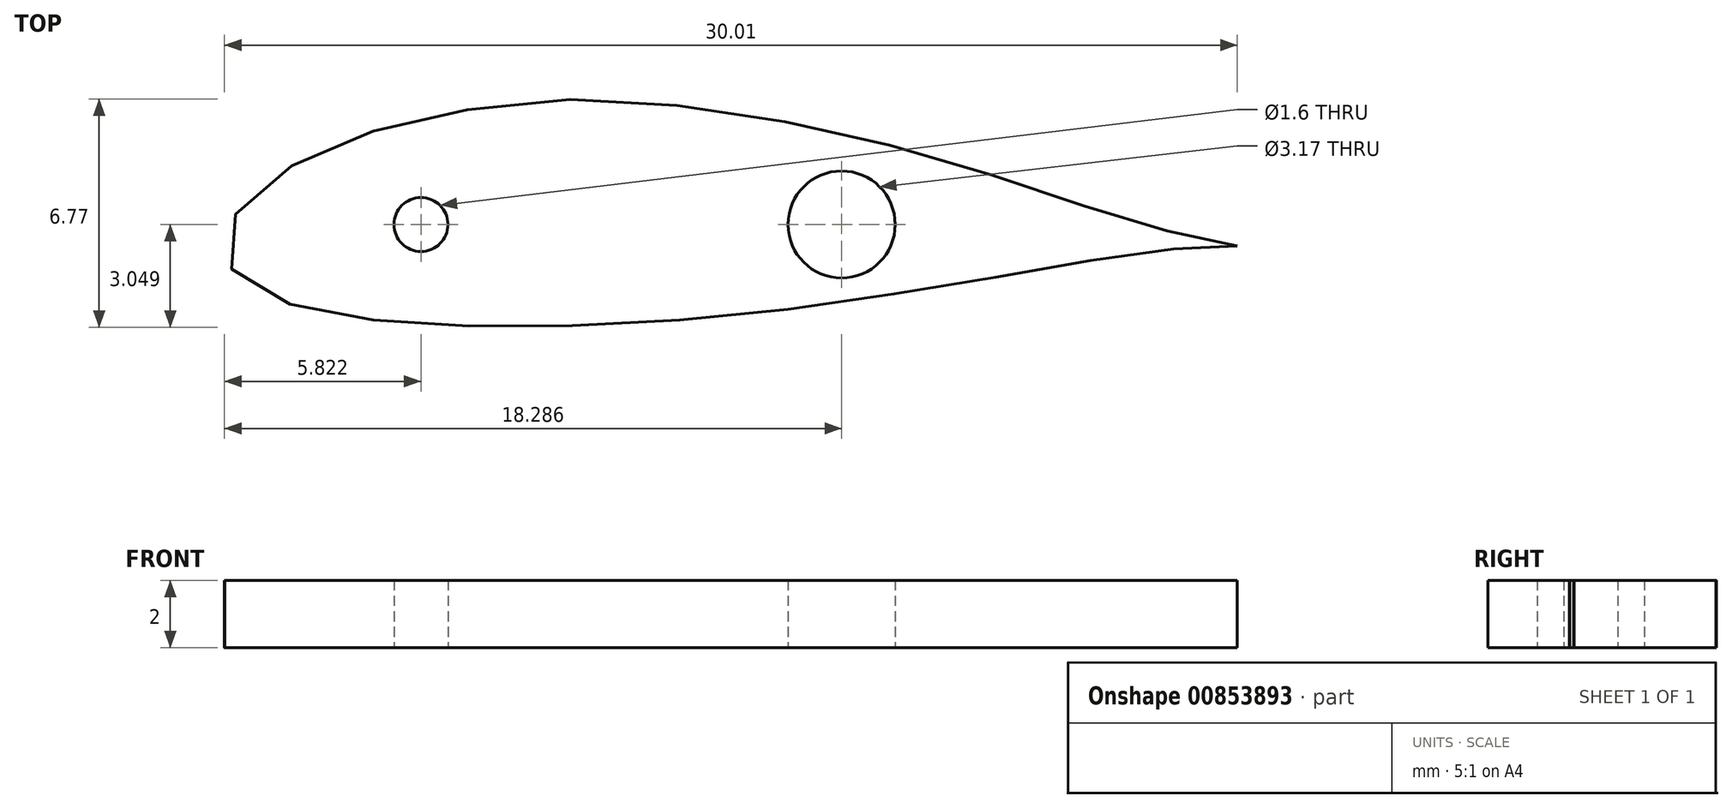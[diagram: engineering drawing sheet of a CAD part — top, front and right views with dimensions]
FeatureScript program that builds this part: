
annotation { "Feature Type Name" : "Feature", "Feature Type Description" : "" }
export const myFeature = defineFeature(function(context is Context, id is Id, definition is map)
    precondition{}
    {
        {
            var Q0;
            Q0=qCreatedBy(makeId("Top.planeOp"),FACE);
            var sketch = newSketch(context, id + "F0", { "sketchPlane" : qUnion([Q0])});
            skPoint(sketch, "E0", {"position": v(-51.28, 25.16) * mm});
            skPoint(sketch, "E1", {"position": v(-51.19, 25.72) * mm});
            skPoint(sketch, "E2", {"position": v(-51.29, 25.4) * mm});
            skPoint(sketch, "E3", {"position": v(-51.02, 26) * mm});
            skPoint(sketch, "E4", {"position": v(-50.8, 26.3) * mm});
            skPoint(sketch, "E5", {"position": v(-50.53, 26.6) * mm});
            skPoint(sketch, "E6", {"position": v(-50.17, 26.92) * mm});
            skPoint(sketch, "E7", {"position": v(-49.77, 27.22) * mm});
            skPoint(sketch, "E8", {"position": v(-49.3, 27.52) * mm});
            skPoint(sketch, "E9", {"position": v(-48.79, 27.8) * mm});
            skPoint(sketch, "E10", {"position": v(-48.2, 28.06) * mm});
            skPoint(sketch, "E11", {"position": v(-47.6, 28.32) * mm});
            skPoint(sketch, "E12", {"position": v(-46.9, 28.55) * mm});
            skPoint(sketch, "E13", {"position": v(-46.2, 28.75) * mm});
            skPoint(sketch, "E14", {"position": v(-45.45, 28.94) * mm});
            skPoint(sketch, "E15", {"position": v(-44.66, 29.1) * mm});
            skPoint(sketch, "E16", {"position": v(-43.83, 29.23) * mm});
            skPoint(sketch, "E17", {"position": v(-42.94, 29.34) * mm});
            skPoint(sketch, "E18", {"position": v(-42.04, 29.5) * mm});
            skPoint(sketch, "E19", {"position": v(-41.14, 29.5) * mm});
            skPoint(sketch, "E20", {"position": v(-40.19, 29.5) * mm});
            skPoint(sketch, "E21", {"position": v(-51.28, 24.9) * mm});
            skPoint(sketch, "E22", {"position": v(-51.18, 24.63) * mm});
            skPoint(sketch, "E23", {"position": v(-51.03, 24.4) * mm});
            skPoint(sketch, "E24", {"position": v(-50.81, 24.16) * mm});
            skPoint(sketch, "E25", {"position": v(-50.51, 23.94) * mm});
            skPoint(sketch, "E26", {"position": v(-50.17, 23.75) * mm});
            skPoint(sketch, "E27", {"position": v(-49.77, 23.56) * mm});
            skPoint(sketch, "E28", {"position": v(-49.3, 23.42) * mm});
            skPoint(sketch, "E29", {"position": v(-48.8, 23.28) * mm});
            skPoint(sketch, "E30", {"position": v(-48.2, 23.13) * mm});
            skPoint(sketch, "E31", {"position": v(-47.6, 23.02) * mm});
            skPoint(sketch, "E32", {"position": v(-46.9, 22.95) * mm});
            skPoint(sketch, "E33", {"position": v(-46.2, 22.89) * mm});
            skPoint(sketch, "E34", {"position": v(-45.45, 22.8) * mm});
            skPoint(sketch, "E35", {"position": v(-40.19, 22.82) * mm});
            skPoint(sketch, "E36", {"position": v(-39.24, 22.87) * mm});
            skPoint(sketch, "E37", {"position": v(-37.31, 29.26) * mm});
            skPoint(sketch, "E38", {"position": v(-36.31, 29.14) * mm});
            skPoint(sketch, "E39", {"position": v(-35.33, 28.94) * mm});
            skPoint(sketch, "E40", {"position": v(-38.27, 22.92) * mm});
            skPoint(sketch, "E41", {"position": v(-37.3, 23) * mm});
            skPoint(sketch, "E42", {"position": v(-36.31, 23.08) * mm});
            skPoint(sketch, "E43", {"position": v(-35.33, 23.2) * mm});
            skPoint(sketch, "E44", {"position": v(-34.33, 23.31) * mm});
            skPoint(sketch, "E45", {"position": v(-33.4, 23.45) * mm});
            skPoint(sketch, "E46", {"position": v(-32.44, 23.56) * mm});
            skPoint(sketch, "E47", {"position": v(-31.48, 23.72) * mm});
            skPoint(sketch, "E48", {"position": v(-30.57, 23.86) * mm});
            skPoint(sketch, "E49", {"position": v(-29.68, 24.04) * mm});
            skPoint(sketch, "E50", {"position": v(-28.81, 24.15) * mm});
            skPoint(sketch, "E51", {"position": v(-34.33, 28.78) * mm});
            skPoint(sketch, "E52", {"position": v(-33.4, 28.6) * mm});
            skPoint(sketch, "E53", {"position": v(-32.41, 28.37) * mm});
            skPoint(sketch, "E54", {"position": v(-31.5, 28.12) * mm});
            skPoint(sketch, "E55", {"position": v(-30.6, 27.85) * mm});
            skPoint(sketch, "E56", {"position": v(-29.68, 27.57) * mm});
            skPoint(sketch, "E57", {"position": v(-28.81, 27.34) * mm});
            skPoint(sketch, "E58", {"position": v(-27.97, 27.02) * mm});
            skPoint(sketch, "E59", {"position": v(-27.2, 26.8) * mm});
            skPoint(sketch, "E60", {"position": v(-28, 24.31) * mm});
            skPoint(sketch, "E61", {"position": v(-27.2, 24.46) * mm});
            skPoint(sketch, "E62", {"position": v(-26.42, 24.57) * mm});
            skPoint(sketch, "E63", {"position": v(-25.73, 24.7) * mm});
            skPoint(sketch, "E64", {"position": v(-25.07, 24.81) * mm});
            skPoint(sketch, "E65", {"position": v(-24.42, 24.9) * mm});
            skPoint(sketch, "E66", {"position": v(-23.86, 24.99) * mm});
            skPoint(sketch, "E67", {"position": v(-23.34, 25.05) * mm});
            skPoint(sketch, "E68", {"position": v(-21.28, 25.16) * mm});
            skPoint(sketch, "E69", {"position": v(-21.47, 25.16) * mm});
            skPoint(sketch, "E70", {"position": v(-21.63, 25.16) * mm});
            skPoint(sketch, "E71", {"position": v(-21.83, 25.16) * mm});
            skPoint(sketch, "E72", {"position": v(-22.14, 25.16) * mm});
            skPoint(sketch, "E73", {"position": v(-22.88, 25.1) * mm});
            skPoint(sketch, "E74", {"position": v(-22.49, 25.13) * mm});
            skPoint(sketch, "E75", {"position": v(-22.49, 25.37) * mm});
            skPoint(sketch, "E76", {"position": v(-22.15, 25.29) * mm});
            skPoint(sketch, "E77", {"position": v(-22.88, 25.47) * mm});
            skPoint(sketch, "E78", {"position": v(-21.86, 25.24) * mm});
            skPoint(sketch, "E79", {"position": v(-21.63, 25.2) * mm});
            skPoint(sketch, "E80", {"position": v(-21.47, 25.18) * mm});
            skPoint(sketch, "E81", {"position": v(-26.45, 26.54) * mm});
            skPoint(sketch, "E82", {"position": v(-25.73, 26.31) * mm});
            skPoint(sketch, "E83", {"position": v(-25.07, 26.1) * mm});
            skPoint(sketch, "E84", {"position": v(-24.44, 25.91) * mm});
            skPoint(sketch, "E85", {"position": v(-23.86, 25.74) * mm});
            skPoint(sketch, "E86", {"position": v(-23.34, 25.59) * mm});
            skPoint(sketch, "E87", {"position": v(-39.26, 29.41) * mm});
            skPoint(sketch, "E88", {"position": v(-38.28, 29.35) * mm});
            skPoint(sketch, "E89", {"position": v(-41.14, 22.79) * mm});
            skPoint(sketch, "E90", {"position": v(-44.67, 22.78) * mm});
            skPoint(sketch, "E91", {"position": v(-43.82, 22.77) * mm});
            skPoint(sketch, "E92", {"position": v(-42.96, 22.74) * mm});
            skPoint(sketch, "E93", {"position": v(-42.05, 22.75) * mm});
            skFitSpline(sketch, "E94", {"points": [v(-21.28, 25.16) * mm, v(-21.47, 25.18) * mm, v(-21.83, 25.16) * mm, v(-22.14, 25.16) * mm, v(-22.49, 25.13) * mm, v(-22.88, 25.1) * mm, v(-23.34, 25.05) * mm, v(-23.86, 24.99) * mm, v(-24.42, 24.9) * mm, v(-25.07, 24.81) * mm, v(-25.73, 24.7) * mm, v(-26.42, 24.57) * mm, v(-27.2, 24.46) * mm, v(-28, 24.31) * mm, v(-28.81, 24.15) * mm, v(-29.68, 24.04) * mm, v(-30.57, 23.86) * mm, v(-31.48, 23.72) * mm, v(-32.44, 23.56) * mm, v(-33.4, 23.45) * mm, v(-34.33, 23.31) * mm, v(-35.33, 23.2) * mm, v(-36.31, 23.08) * mm, v(-37.3, 23) * mm, v(-38.27, 22.92) * mm, v(-39.24, 22.87) * mm, v(-40.19, 22.82) * mm, v(-41.14, 22.79) * mm, v(-42.05, 22.75) * mm, v(-42.96, 22.74) * mm, v(-43.82, 22.77) * mm, v(-44.67, 22.78) * mm, v(-45.45, 22.8) * mm, v(-46.2, 22.89) * mm, v(-46.9, 22.95) * mm, v(-47.6, 23.02) * mm, v(-48.2, 23.13) * mm, v(-48.8, 23.28) * mm, v(-49.3, 23.42) * mm, v(-49.77, 23.56) * mm, v(-50.17, 23.75) * mm, v(-50.51, 23.94) * mm, v(-50.81, 24.16) * mm, v(-51.03, 24.4) * mm, v(-51.18, 24.63) * mm, v(-51.28, 24.9) * mm, v(-51.28, 25.16) * mm, v(-51.29, 25.4) * mm, v(-51.19, 25.72) * mm, v(-51.02, 26) * mm, v(-50.8, 26.3) * mm, v(-50.53, 26.6) * mm, v(-50.17, 26.92) * mm, v(-49.77, 27.22) * mm, v(-49.3, 27.52) * mm, v(-48.79, 27.8) * mm, v(-48.2, 28.06) * mm, v(-47.6, 28.32) * mm, v(-46.9, 28.55) * mm, v(-46.2, 28.75) * mm, v(-45.45, 28.94) * mm, v(-44.66, 29.1) * mm, v(-43.83, 29.23) * mm, v(-42.94, 29.34) * mm, v(-42.04, 29.5) * mm, v(-41.14, 29.5) * mm, v(-40.19, 29.5) * mm, v(-39.26, 29.41) * mm, v(-38.28, 29.35) * mm, v(-37.31, 29.26) * mm, v(-36.31, 29.14) * mm, v(-35.33, 28.94) * mm, v(-34.33, 28.78) * mm, v(-33.4, 28.6) * mm, v(-32.41, 28.37) * mm, v(-31.5, 28.12) * mm, v(-30.6, 27.85) * mm, v(-29.68, 27.57) * mm, v(-28.81, 27.34) * mm, v(-27.97, 27.02) * mm, v(-27.2, 26.8) * mm, v(-26.45, 26.54) * mm, v(-25.73, 26.31) * mm, v(-25.07, 26.1) * mm, v(-24.44, 25.91) * mm, v(-23.86, 25.74) * mm, v(-23.34, 25.59) * mm, v(-22.88, 25.47) * mm, v(-22.49, 25.37) * mm, v(-22.15, 25.29) * mm, v(-21.86, 25.29) * mm, v(-21.28, 25.16) * mm]});
            skCircle(sketch, "E95", {"center": v(-45.47, 25.79) * mm, "radius": 0.8 * mm});
            skCircle(sketch, "E96", {"center": v(-33, 25.79) * mm, "radius": 1.59 * mm});
            skSolve(sketch);
        }
        {
            var Q0;
            Q0=makeQuery(id+"F0.imprint","IMPRINT",FACE,{"disambiguationData":[TD([[makeQuery(id+"F0.imprint","IMPRINT",EDGE,{"derivedFrom":sQuery(id+"F0.wireOp",EDGE,"E94")}),-1.0]])]});
            extrude(context, id + "F1", {"entities" : qUnion([Q0]), "depth" : 2 * mm, "offsetDistance" : 25.4 * mm});
        }
    });
